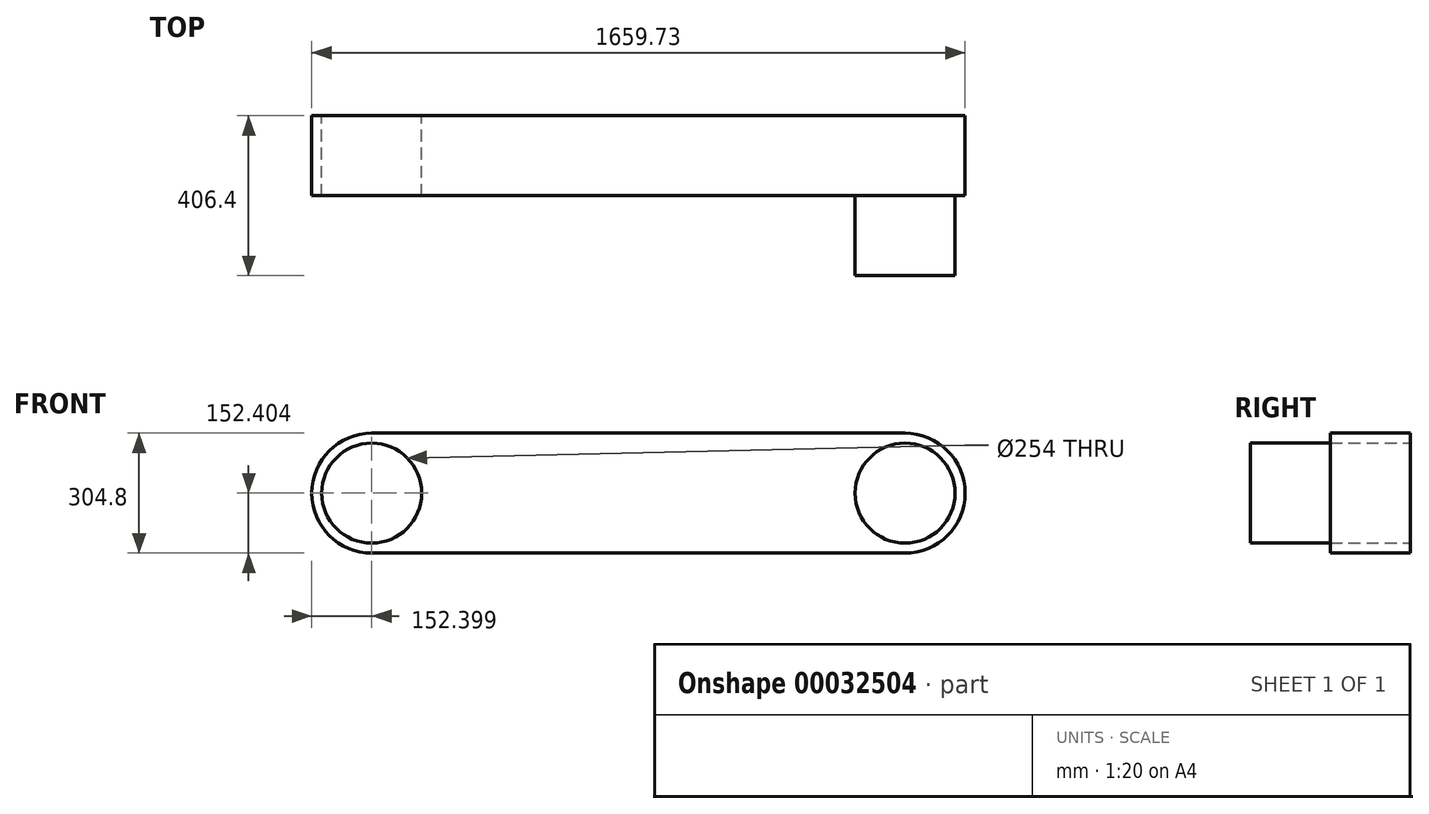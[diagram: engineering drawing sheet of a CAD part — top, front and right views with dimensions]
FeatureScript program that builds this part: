
annotation { "Feature Type Name" : "Feature", "Feature Type Description" : "" }
export const myFeature = defineFeature(function(context is Context, id is Id, definition is map)
    precondition{}
    {
        {
            var Q0;
            Q0=qCreatedBy(makeId("Front.planeOp"),FACE);
            var sketch = newSketch(context, id + "F0", { "sketchPlane" : qUnion([Q0])});
            skLineSegment(sketch, "E0.left", {"start": v(-670.17, 114.48) * mm, "end": v(-670.17, -139.52) * mm});
            skLineSegment(sketch, "E0.right", {"start": v(684.76, 114.48) * mm, "end": v(684.76, -139.52) * mm});
            skCircle(sketch, "E1", {"center": v(-670.17, -12.52) * mm, "radius": 127 * mm});
            skCircle(sketch, "E2", {"center": v(684.76, -12.52) * mm, "radius": 127 * mm});
            skLineSegment(sketch, "E3", {"start": v(-670.17, -139.52) * mm, "end": v(-670.17, -164.92) * mm});
            skLineSegment(sketch, "E4", {"start": v(-670.17, -164.92) * mm, "end": v(684.76, -164.92) * mm});
            skLineSegment(sketch, "E5", {"start": v(684.76, -164.92) * mm, "end": v(684.76, -139.52) * mm});
            skLineSegment(sketch, "E6", {"start": v(-670.17, 114.48) * mm, "end": v(-670.17, 139.88) * mm});
            skLineSegment(sketch, "E7", {"start": v(-670.17, 139.88) * mm, "end": v(684.76, 139.88) * mm});
            skLineSegment(sketch, "E8", {"start": v(684.76, 139.88) * mm, "end": v(684.76, 114.48) * mm});
            skArc(sketch, "E9", {"start": v(-670.17, 139.88) * mm, "mid": v(-822.57, -12.52) * mm, "end": v(-670.17, -164.92) * mm});
            skArc(sketch, "E10", {"start": v(684.76, -164.92) * mm, "mid": v(837.16, -12.52) * mm, "end": v(684.76, 139.88) * mm});
            skSolve(sketch);
        }
        {
            var Q0;
            Q0 = qSketchRegion(id + "F0", true);
            extrude(context, id + "F1", {"entities" : qUnion([Q0]), "depth" : 203.2 * mm});
        }
        {
            var Q0;
            {var subQ0=sQuery(id+"F0.wireOp",EDGE,"E2");var subQ1=sQuery(id+"F0.wireOp",EDGE,"E0.right");var subQ3=makeQuery(id+"F0.imprint","INTERSECT",VERTEX,{"disambiguationData":[OD(0.0)],"derivedFrom":[subQ1,subQ0]});Q0=makeQuery(id+"F0.imprint","IMPRINT",FACE,{"disambiguationData":[TD([[makeQuery(id+"F0.imprint","IMPRINT",EDGE,{"disambiguationData":[TD([[subQ3,-1.0]])],"derivedFrom":subQ1}),1.0]])]});}
            var Q1;
            {var subQ0=sQuery(id+"F0.wireOp",EDGE,"E2");var subQ1=sQuery(id+"F0.wireOp",EDGE,"E0.right");var subQ3=makeQuery(id+"F0.imprint","INTERSECT",VERTEX,{"disambiguationData":[OD(0.0)],"derivedFrom":[subQ1,subQ0]});Q1=makeQuery(id+"F0.imprint","IMPRINT",FACE,{"disambiguationData":[TD([[makeQuery(id+"F0.imprint","IMPRINT",EDGE,{"disambiguationData":[TD([[subQ3,-1.0]])],"derivedFrom":subQ1}),-1.0]])]});}
            extrude(context, id + "F2", {"entities" : qUnion([Q0, Q1]), "operationType" : NewBodyOperationType.ADD, "depth" : 406.4 * mm});
        }
    });
